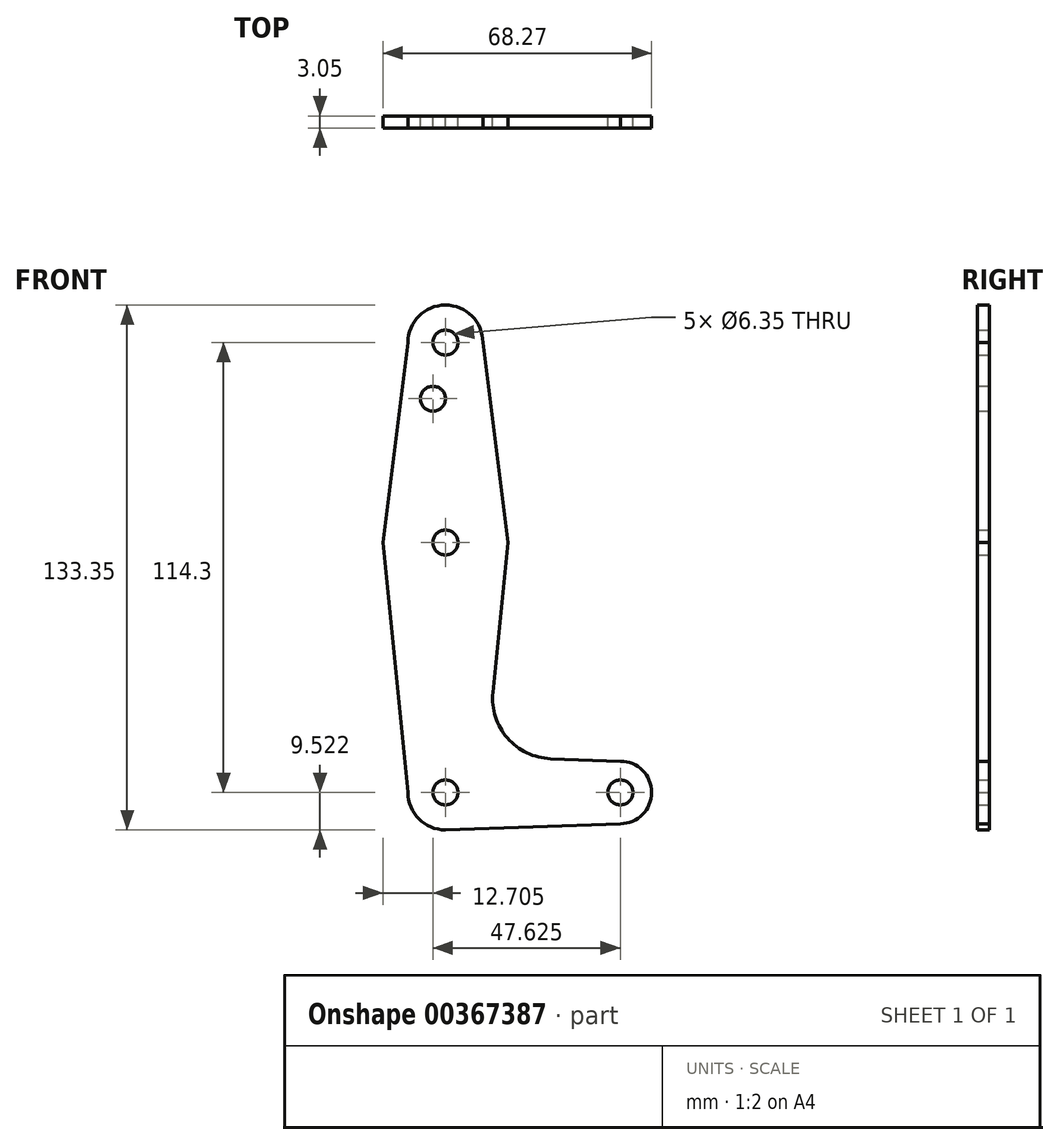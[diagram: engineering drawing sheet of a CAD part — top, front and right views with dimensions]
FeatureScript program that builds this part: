
annotation { "Feature Type Name" : "Feature", "Feature Type Description" : "" }
export const myFeature = defineFeature(function(context is Context, id is Id, definition is map)
    precondition{}
    {
        {
            var Q0;
            Q0=qCreatedBy(makeId("Front.planeOp"),FACE);
            var sketch = newSketch(context, id + "F0", { "sketchPlane" : qUnion([Q0])});
            skCircle(sketch, "E0", {"center": v(0, 82.14) * mm, "radius": 9.53 * mm});
            skCircle(sketch, "E1", {"center": v(0, 31.34) * mm, "radius": 15.88 * mm});
            skCircle(sketch, "E2", {"center": v(0, -32.16) * mm, "radius": 9.53 * mm});
            skCircle(sketch, "E3", {"center": v(44.45, -32.16) * mm, "radius": 7.94 * mm});
            skLineSegment(sketch, "E4", {"start": v(0, 82.14) * mm, "end": v(0, -32.16) * mm, "construction": true});
            skLineSegment(sketch, "E5", {"start": v(44.45, -32.16) * mm, "end": v(0, -32.16) * mm, "construction": true});
            skLineSegment(sketch, "E6", {"start": v(-9.53, 82.14) * mm, "end": v(-15.88, 31.34) * mm});
            skLineSegment(sketch, "E7", {"start": v(-15.88, 31.34) * mm, "end": v(-9.53, -32.16) * mm});
            skLineSegment(sketch, "E8", {"start": v(9.52, 82.14) * mm, "end": v(15.87, 31.34) * mm});
            skLineSegment(sketch, "E9", {"start": v(0, -41.68) * mm, "end": v(44.45, -40.1) * mm});
            skLineSegment(sketch, "E10", {"start": v(15.87, 31.34) * mm, "end": v(12.06, -6.78) * mm});
            skLineSegment(sketch, "E11", {"start": v(44.45, -24.22) * mm, "end": v(26.74, -23.59) * mm});
            skCircle(sketch, "E12", {"center": v(0, 82.14) * mm, "radius": 3.18 * mm});
            skCircle(sketch, "E13", {"center": v(0, 31.34) * mm, "radius": 3.18 * mm});
            skCircle(sketch, "E14", {"center": v(0, -32.16) * mm, "radius": 3.18 * mm});
            skCircle(sketch, "E15", {"center": v(44.45, -32.16) * mm, "radius": 3.18 * mm});
            skCircle(sketch, "E16", {"center": v(-3.17, 67.87) * mm, "radius": 3.18 * mm});
            skArc(sketch, "E17.filletArc", {"start": v(12.06, -6.78) * mm, "mid": v(15.76, -18.36) * mm, "end": v(26.74, -23.59) * mm});
            skSolve(sketch);
        }
        {
            var Q0;
            Q0=makeQuery(id+"F0.imprint","IMPRINT",FACE,{"disambiguationData":[TD([[makeQuery(id+"F0.imprint","IMPRINT",EDGE,{"derivedFrom":sQuery(id+"F0.wireOp",EDGE,"E12")}),-1.0]])]});
            var Q1;
            Q1=makeQuery(id+"F0.imprint","IMPRINT",FACE,{"disambiguationData":[TD([[makeQuery(id+"F0.imprint","IMPRINT",EDGE,{"derivedFrom":sQuery(id+"F0.wireOp",EDGE,"E16")}),-1.0]])]});
            var Q2;
            Q2=makeQuery(id+"F0.imprint","IMPRINT",FACE,{"disambiguationData":[TD([[makeQuery(id+"F0.imprint","IMPRINT",EDGE,{"derivedFrom":sQuery(id+"F0.wireOp",EDGE,"E13")}),-1.0]])]});
            var Q3;
            {var subQ9=sQuery(id+"F0.wireOp",EDGE,"E11");Q3=makeQuery(id+"F0.imprint","IMPRINT",FACE,{"disambiguationData":[TD([[makeQuery(id+"F0.imprint","IMPRINT",EDGE,{"derivedFrom":subQ9}),1.0]])]});}
            var Q4;
            Q4=makeQuery(id+"F0.imprint","IMPRINT",FACE,{"disambiguationData":[TD([[makeQuery(id+"F0.imprint","IMPRINT",EDGE,{"derivedFrom":sQuery(id+"F0.wireOp",EDGE,"E14")}),-1.0]])]});
            var Q5;
            Q5=makeQuery(id+"F0.imprint","IMPRINT",FACE,{"disambiguationData":[TD([[makeQuery(id+"F0.imprint","IMPRINT",EDGE,{"derivedFrom":sQuery(id+"F0.wireOp",EDGE,"E15")}),-1.0]])]});
            extrude(context, id + "F1", {"entities" : qUnion([Q0, Q1, Q2, Q3, Q4, Q5]), "depth" : 3.05 * mm});
        }
    });
